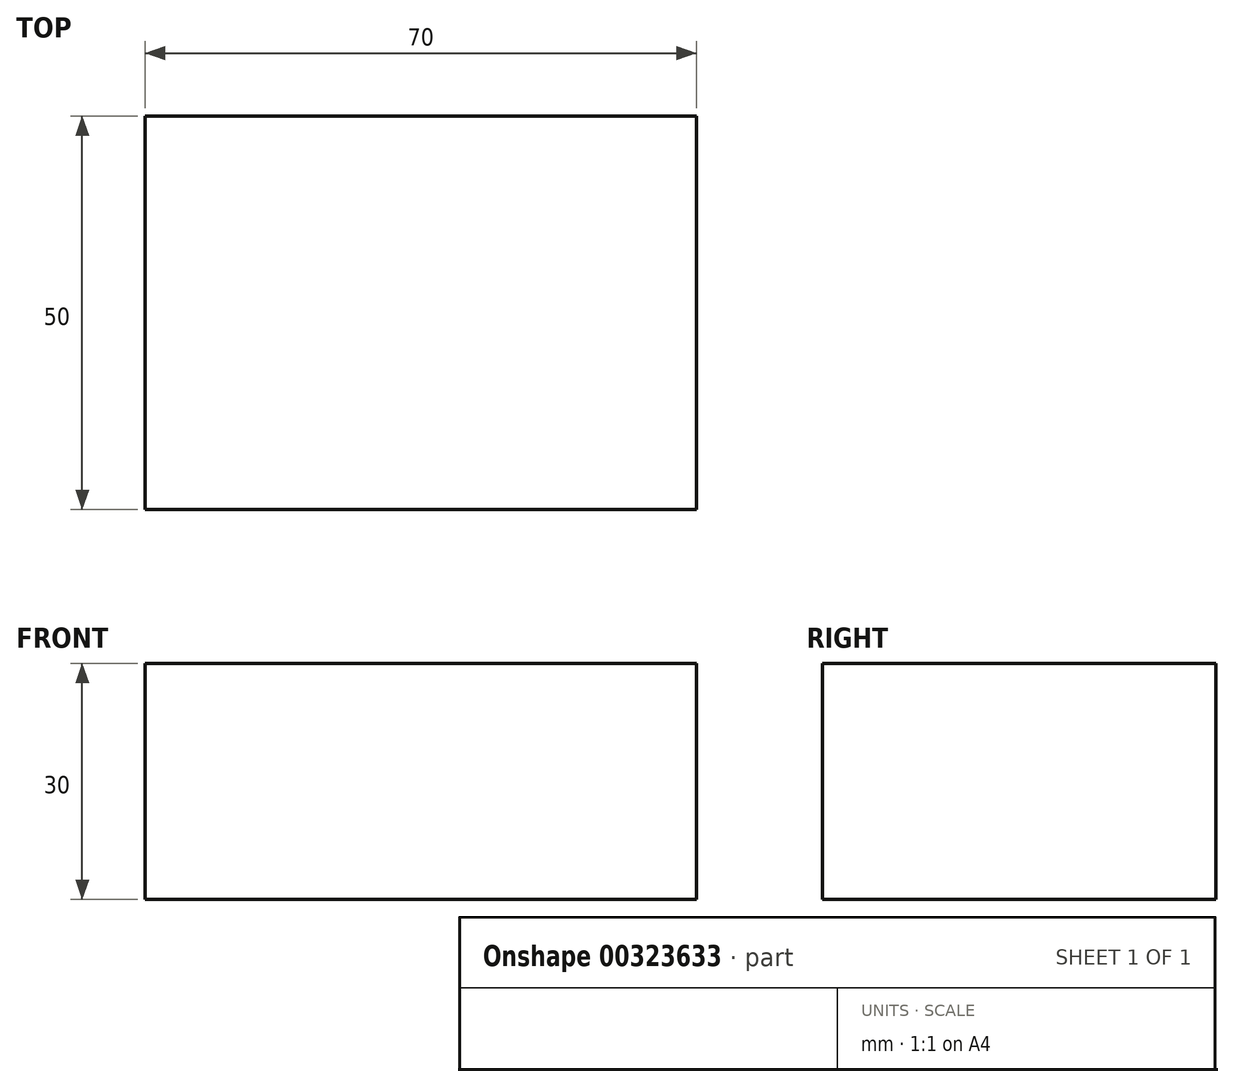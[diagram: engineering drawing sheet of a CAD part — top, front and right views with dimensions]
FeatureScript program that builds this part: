
annotation { "Feature Type Name" : "Feature", "Feature Type Description" : "" }
export const myFeature = defineFeature(function(context is Context, id is Id, definition is map)
    precondition{}
    {
        {
            var Q0;
            Q0=qCreatedBy(makeId("Top.planeOp"),FACE);
            var sketch = newSketch(context, id + "F0", { "sketchPlane" : qUnion([Q0])});
            skLineSegment(sketch, "E0.bottom", {"start": v(0, 0) * mm, "end": v(70, 0) * mm});
            skLineSegment(sketch, "E0.top", {"start": v(0, 50) * mm, "end": v(70, 50) * mm});
            skLineSegment(sketch, "E0.left", {"start": v(0, 0) * mm, "end": v(0, 50) * mm});
            skLineSegment(sketch, "E0.right", {"start": v(70, 0) * mm, "end": v(70, 50) * mm});
            skSolve(sketch);
        }
        {
            var Q0;
            Q0 = qSketchRegion(id + "F0", true);
            extrude(context, id + "F1", {"entities" : qUnion([Q0]), "depth" : 30 * mm});
        }
    });
